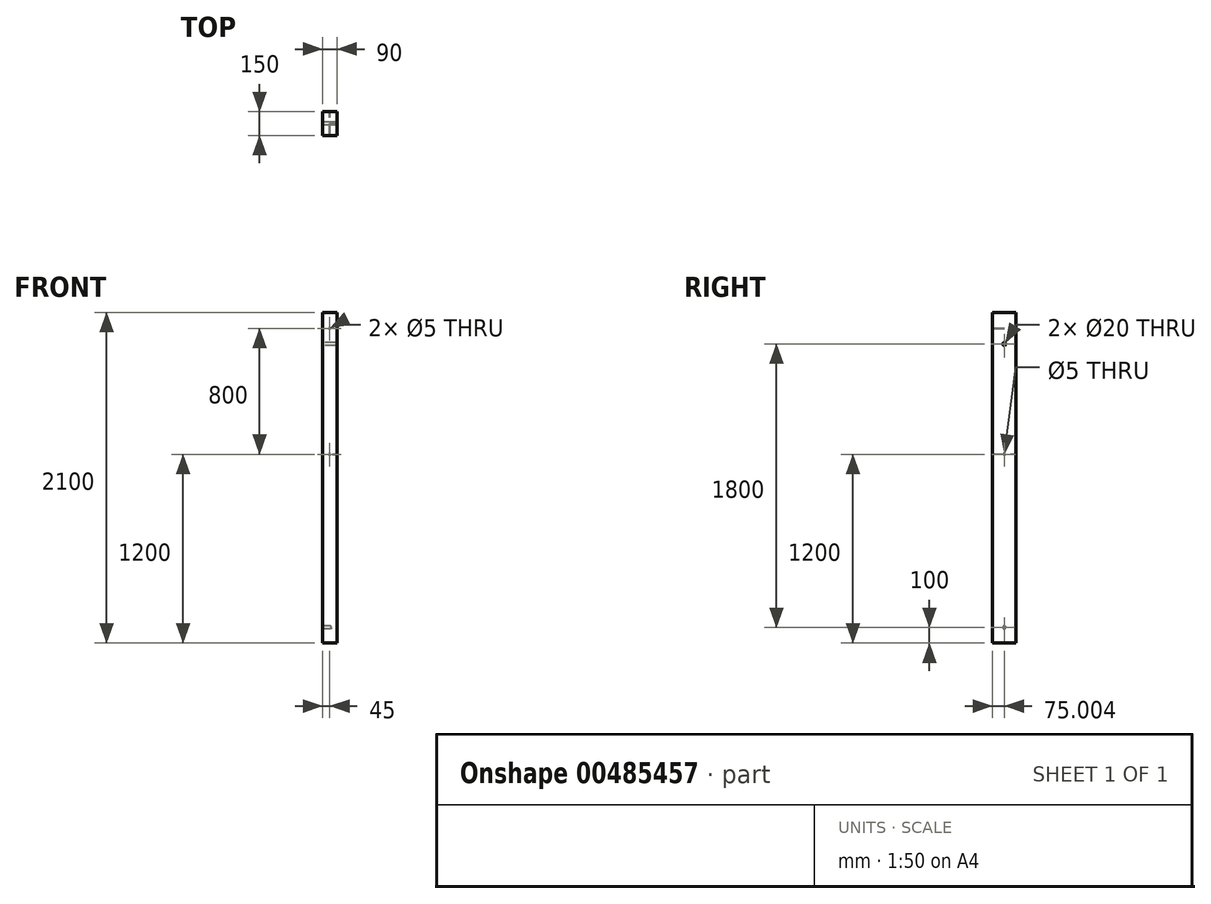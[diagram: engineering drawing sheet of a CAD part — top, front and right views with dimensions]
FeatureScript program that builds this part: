
annotation { "Feature Type Name" : "Feature", "Feature Type Description" : "" }
export const myFeature = defineFeature(function(context is Context, id is Id, definition is map)
    precondition{}
    {
        {
            var Q0;
            Q0=qCreatedBy(makeId("Top.planeOp"),FACE);
            var sketch = newSketch(context, id + "F0", { "sketchPlane" : qUnion([Q0])});
            skLineSegment(sketch, "E0.bottom", {"start": v(-45, 141.65) * mm, "end": v(45, 141.65) * mm});
            skLineSegment(sketch, "E0.top", {"start": v(-45, -8.35) * mm, "end": v(45, -8.35) * mm});
            skLineSegment(sketch, "E0.left", {"start": v(-45, 141.65) * mm, "end": v(-45, -8.35) * mm});
            skLineSegment(sketch, "E0.right", {"start": v(45, 141.65) * mm, "end": v(45, -8.35) * mm});
            skPoint(sketch, "E0.middle", {"position": v(0, 66.65) * mm});
            skLineSegment(sketch, "E1.bottom", {"start": v(34.26, 141.65) * mm, "end": v(-34.26, 141.65) * mm});
            skLineSegment(sketch, "E1.top", {"start": v(34.26, 141.65) * mm, "end": v(-34.26, 141.65) * mm});
            skLineSegment(sketch, "E1.left", {"start": v(34.26, 141.65) * mm, "end": v(34.26, 141.65) * mm});
            skLineSegment(sketch, "E1.right", {"start": v(-34.26, 141.65) * mm, "end": v(-34.26, 141.65) * mm});
            skPoint(sketch, "E1.middle", {"position": v(0, 141.65) * mm});
            skSolve(sketch);
        }
        {
            var Q0;
            Q0=makeQuery(id+"F0.imprint","IMPRINT",FACE,{"disambiguationData":[TD([[makeQuery(id+"F0.imprint","IMPRINT",EDGE,{"derivedFrom":sQuery(id+"F0.wireOp",EDGE,"E0.top")}),1.0]])]});
            extrude(context, id + "F1", {"entities" : qUnion([Q0]), "depth" : 2100 * mm});
        }
        {
            var Q0;
            Q0=makeQuery(id+"F1.opExtrude","SWEPT_FACE",FACE,{"disambiguationData":[OSD([sQuery(id+"F0.wireOp",EDGE,"E0.right")])]});
            var sketch = newSketch(context, id + "F2", { "sketchPlane" : qUnion([Q0])});
            skPoint(sketch, "E2", {"position": v(66.65, 1200) * mm});
            skSolve(sketch);
        }
        {
            var Q0;
            Q0=sQuery(id+"F2.wireOp",VERTEX,"E2");
            var Q1;
            Q1=makeQuery(id+"F1.opExtrude","SWEPT_BODY",BODY,{"disambiguationData":[OSD([sQuery(id+"F0.wireOp",EDGE,"E0.bottom"),sQuery(id+"F0.wireOp",EDGE,"E0.top"),sQuery(id+"F0.wireOp",EDGE,"E0.left"),sQuery(id+"F0.wireOp",EDGE,"E0.right"),sQuery(id+"F0.wireOp",EDGE,"E1.top")])]});
            hole(context, id + "F3", {"style" : HoleStyle.SIMPLE, "endStyle" : HoleEndStyle.BLIND, "holeDiameter" : 5 * mm, "holeDepth" : 25 * mm, "isTappedThrough" : true, "tappedDepth" : 12 * mm, "tapClearance" : 3, "locations" : qUnion([Q0]), "scope" : qUnion([Q1])});
        }
        {
            var Q0;
            Q0=makeQuery(id+"F1.opExtrude","SWEPT_FACE",FACE,{"disambiguationData":[OSD([sQuery(id+"F0.wireOp",EDGE,"E0.bottom"),sQuery(id+"F0.wireOp",EDGE,"E1.top")])]});
            var sketch = newSketch(context, id + "F4", { "sketchPlane" : qUnion([Q0])});
            skPoint(sketch, "E3", {"position": v(0, 2000) * mm});
            skPoint(sketch, "E4", {"position": v(0, 1200) * mm});
            skSolve(sketch);
        }
        {
            var Q0;
            Q0=sQuery(id+"F4.wireOp",VERTEX,"E3");
            var Q1;
            Q1=makeQuery(id+"F1.opExtrude","SWEPT_BODY",BODY,{"disambiguationData":[OSD([sQuery(id+"F0.wireOp",EDGE,"E0.bottom"),sQuery(id+"F0.wireOp",EDGE,"E0.top"),sQuery(id+"F0.wireOp",EDGE,"E0.left"),sQuery(id+"F0.wireOp",EDGE,"E0.right"),sQuery(id+"F0.wireOp",EDGE,"E1.top")])]});
            hole(context, id + "F5", {"style" : HoleStyle.SIMPLE, "endStyle" : HoleEndStyle.THROUGH, "holeDiameter" : 5 * mm, "isTappedThrough" : true, "tappedDepth" : 12 * mm, "tapClearance" : 3, "locations" : qUnion([Q0]), "scope" : qUnion([Q1])});
        }
        {
            var Q0;
            Q0=sQuery(id+"F4.wireOp",VERTEX,"E4");
            var Q1;
            Q1=makeQuery(id+"F1.opExtrude","SWEPT_BODY",BODY,{"disambiguationData":[OSD([sQuery(id+"F0.wireOp",EDGE,"E0.bottom"),sQuery(id+"F0.wireOp",EDGE,"E0.top"),sQuery(id+"F0.wireOp",EDGE,"E0.left"),sQuery(id+"F0.wireOp",EDGE,"E0.right"),sQuery(id+"F0.wireOp",EDGE,"E1.top")])]});
            hole(context, id + "F6", {"style" : HoleStyle.SIMPLE, "endStyle" : HoleEndStyle.THROUGH, "holeDiameter" : 5 * mm, "isTappedThrough" : true, "tappedDepth" : 12 * mm, "tapClearance" : 3, "locations" : qUnion([Q0]), "scope" : qUnion([Q1])});
        }
        {
            var Q0;
            Q0=makeQuery(id+"F1.opExtrude","SWEPT_FACE",FACE,{"disambiguationData":[OSD([sQuery(id+"F0.wireOp",EDGE,"E0.left")])]});
            var sketch = newSketch(context, id + "F7", { "sketchPlane" : qUnion([Q0])});
            skPoint(sketch, "E5", {"position": v(-66.65, 1900) * mm});
            skPoint(sketch, "E6", {"position": v(-66.65, 100) * mm});
            skSolve(sketch);
        }
        {
            var Q0;
            Q0=sQuery(id+"F7.wireOp",VERTEX,"E5");
            var Q1;
            Q1=makeQuery(id+"F1.opExtrude","SWEPT_BODY",BODY,{"disambiguationData":[OSD([sQuery(id+"F0.wireOp",EDGE,"E0.bottom"),sQuery(id+"F0.wireOp",EDGE,"E0.top"),sQuery(id+"F0.wireOp",EDGE,"E0.left"),sQuery(id+"F0.wireOp",EDGE,"E0.right"),sQuery(id+"F0.wireOp",EDGE,"E1.top")])]});
            hole(context, id + "F8", {"style" : HoleStyle.SIMPLE, "endStyle" : HoleEndStyle.THROUGH, "holeDiameter" : 20 * mm, "isTappedThrough" : true, "tappedDepth" : 12 * mm, "tapClearance" : 3, "locations" : qUnion([Q0]), "scope" : qUnion([Q1])});
        }
        {
            var Q0;
            Q0=sQuery(id+"F7.wireOp",VERTEX,"E6");
            var Q1;
            Q1=makeQuery(id+"F1.opExtrude","SWEPT_BODY",BODY,{"disambiguationData":[OSD([sQuery(id+"F0.wireOp",EDGE,"E0.bottom"),sQuery(id+"F0.wireOp",EDGE,"E0.top"),sQuery(id+"F0.wireOp",EDGE,"E0.left"),sQuery(id+"F0.wireOp",EDGE,"E0.right"),sQuery(id+"F0.wireOp",EDGE,"E1.top")])]});
            hole(context, id + "F9", {"style" : HoleStyle.SIMPLE, "endStyle" : HoleEndStyle.BLIND, "holeDiameter" : 20 * mm, "holeDepth" : 50 * mm, "isTappedThrough" : true, "tappedDepth" : 12 * mm, "tapClearance" : 3, "locations" : qUnion([Q0]), "scope" : qUnion([Q1])});
        }
    });
